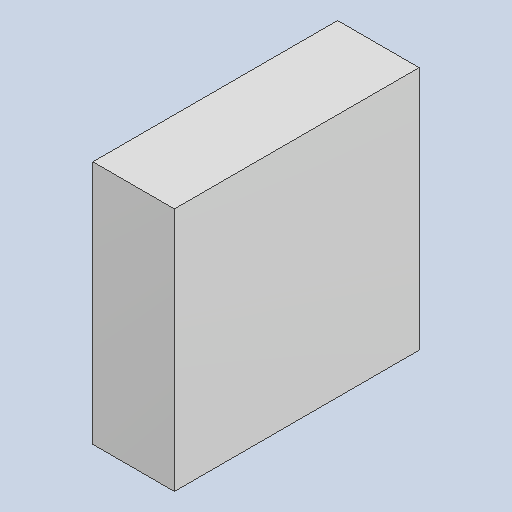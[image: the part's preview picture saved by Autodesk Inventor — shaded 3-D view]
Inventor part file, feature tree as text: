
AUTODESK INVENTOR PART (.ipt)
format: ipt  version: 2023.4 (Build 274418000, 418)  size: 81,408 bytes
history: native  units: mm
features: extrude x1
ambient origin geometry x8: Origin, YZ Plane, XZ Plane, XY Plane, X Axis, Y Axis, Z Axis, Center Point
bodies: Solid1 (feature_tree)
feature tree (1):
  extrude  "Extruded_41"  [1 undecoded]
note: 1 required parameter value undecoded (feature->parameter linkage not recoverable at this tier; creation-order binding heuristic only, values carry confidence <= 0.55)
